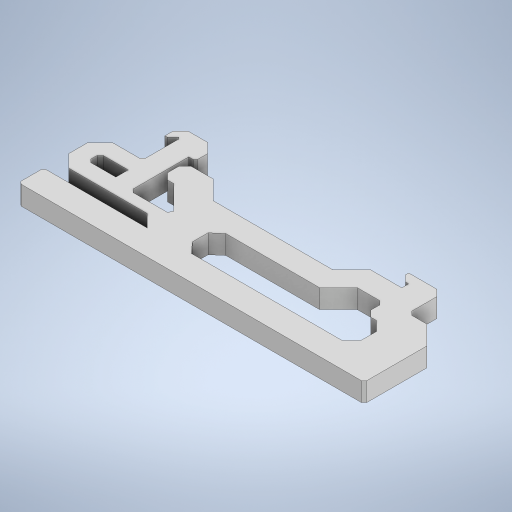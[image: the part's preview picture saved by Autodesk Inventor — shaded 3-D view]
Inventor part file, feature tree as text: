
AUTODESK INVENTOR PART (.ipt)
format: ipt  version: 2024 (Build 280153000, 153)  size: 385,536 bytes
history: native  units: in
note: dims shown in document units (in); Inventor stores cm internally (conversion verified against a paired STEP export)
features: extrude x1
ambient origin geometry x8: Origin, YZ Plane, XZ Plane, XY Plane, X Axis, Y Axis, Z Axis, Center Point
bodies: Solid1 (feature_tree)
feature tree (1):
  extrude  "Extrusion1"  Depth=0.3758in
